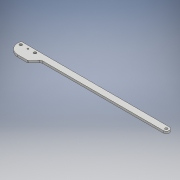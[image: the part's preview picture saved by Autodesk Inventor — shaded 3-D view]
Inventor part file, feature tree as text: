
AUTODESK INVENTOR PART (.ipt)
format: ipt  version: 2018 (Build 220112000, 112)  size: 172,032 bytes
history: native  units: mm
features: extrude x8, sketch x5, fillet x2, projected_geometry x1
ambient origin geometry x8: Origin, YZ Plane, XZ Plane, XY Plane, X Axis, Y Axis, Z Axis, Center Point
bodies: Solid1 (feature_tree)
feature tree (16):
  extrude  "Extrusion1"  Depth=3.683mm
  fillet  "Fillet1"  Radius=3.683mm
  extrude  "Extrusion2"  Depth=23.387412mm
  extrude  "Extrusion3"  Depth=2.0mm
  extrude  "Extrusion4"  Depth=3.0mm TaperAngle=0.0deg
  extrude  "Extrusion5"  Depth=10.0mm TaperAngle=0.0deg
  extrude  "Extrusion6"  Depth=2.0mm
  fillet  "Fillet2"  Radius=6.0mm
  extrude  "Extrusion7"  Depth=10.0mm
  extrude  "Extrusion8"  Depth=10.0mm TaperAngle=0.0deg
  sketch  "Sketch1"  dims[d0=27.94mm d1=3.683mm d2=3.683mm]
  sketch  "Sketch3"  dims[d3=5.0mm d5=23.387412mm]
  sketch  "Sketch4"  dims[d6=3.0mm d7=0.0mm d8=2.0mm]
  sketch  "Sketch5"  dims[d9=8.5mm d10=3.0mm d11=0.0mm]
  projected_geometry  "Projected Loop1"
  sketch  "Sketch6"  dims[d12=3.0mm d13=0.0mm d14=6.0mm d15=0.0mm d16=2.0mm d17=6.0mm d18=0.0mm d19=190.5mm d20=10.0mm d21=0.0mm d22=4.0mm d23=3.556mm d24=10.0mm d25=0.0mm d26=0.0mm d27=10.0mm d28=0.0mm]
